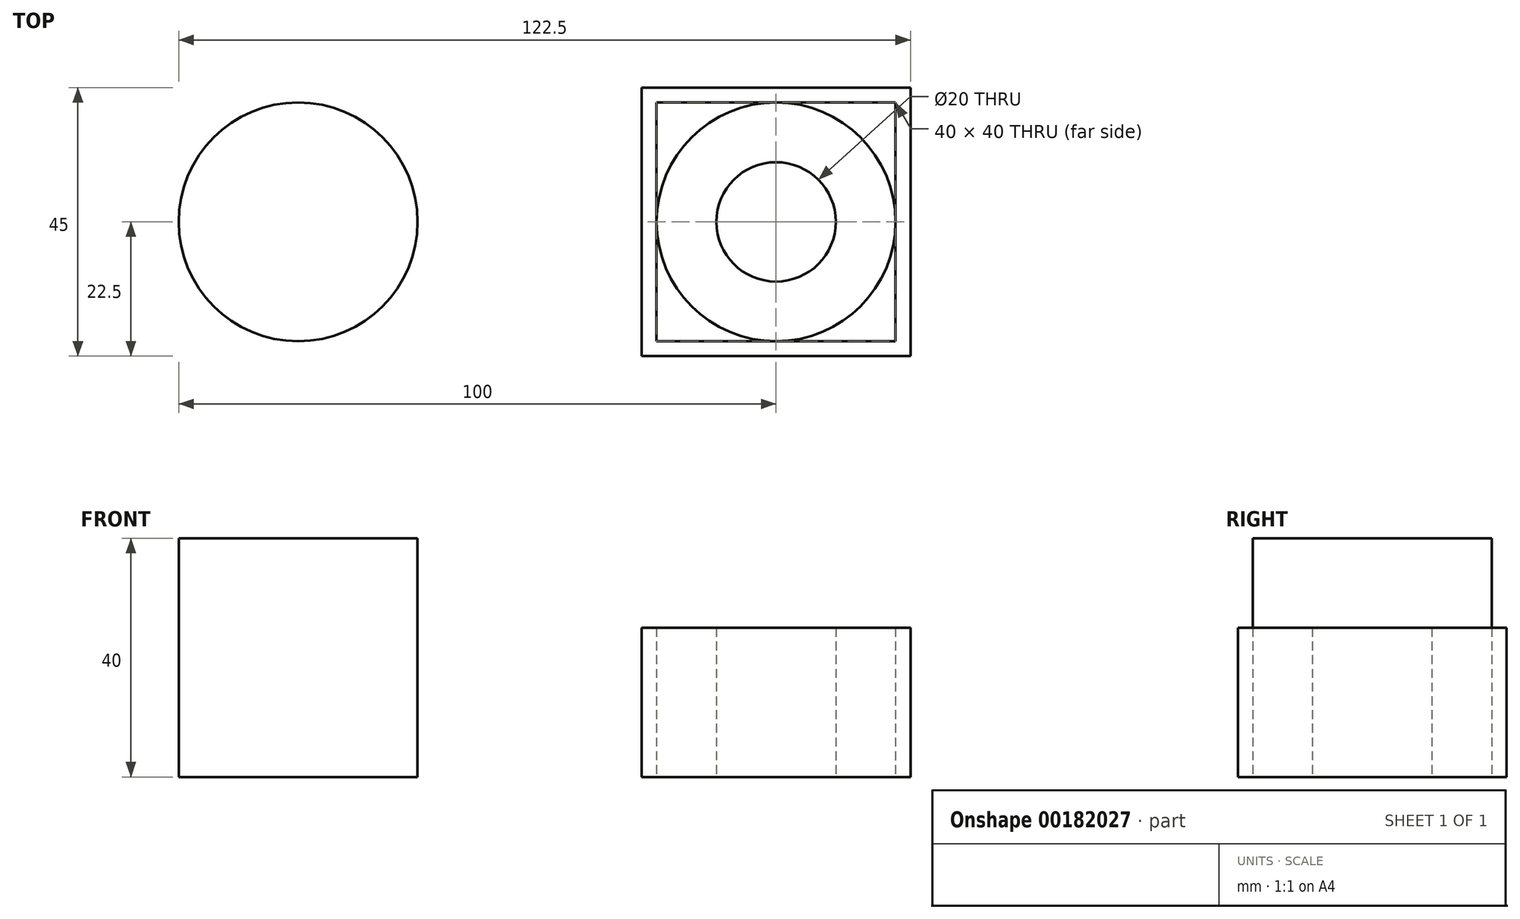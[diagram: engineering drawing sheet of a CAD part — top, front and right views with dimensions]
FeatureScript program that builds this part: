
annotation { "Feature Type Name" : "Feature", "Feature Type Description" : "" }
export const myFeature = defineFeature(function(context is Context, id is Id, definition is map)
    precondition{}
    {
        {
            var Q0;
            Q0=qCreatedBy(makeId("Top.planeOp"),FACE);
            var sketch = newSketch(context, id + "F0", { "sketchPlane" : qUnion([Q0])});
            skCircle(sketch, "E0", {"center": v(0, 0) * mm, "radius": 20 * mm});
            skCircle(sketch, "E1", {"center": v(80, 0) * mm, "radius": 20 * mm});
            skLineSegment(sketch, "E2.bottom", {"start": v(57.5, 22.5) * mm, "end": v(102.5, 22.5) * mm});
            skLineSegment(sketch, "E2.top", {"start": v(57.5, -22.5) * mm, "end": v(102.5, -22.5) * mm});
            skLineSegment(sketch, "E2.left", {"start": v(57.5, 22.5) * mm, "end": v(57.5, -22.5) * mm});
            skLineSegment(sketch, "E2.right", {"start": v(102.5, 22.5) * mm, "end": v(102.5, -22.5) * mm});
            skCircle(sketch, "E3", {"center": v(80, 0) * mm, "radius": 10 * mm});
            skLineSegment(sketch, "E4.bottom", {"start": v(60, 20) * mm, "end": v(100, 20) * mm});
            skLineSegment(sketch, "E4.top", {"start": v(60, -20) * mm, "end": v(100, -20) * mm});
            skLineSegment(sketch, "E4.left", {"start": v(60, 20) * mm, "end": v(60, -20) * mm});
            skLineSegment(sketch, "E4.right", {"start": v(100, 20) * mm, "end": v(100, -20) * mm});
            skSolve(sketch);
        }
        {
            var Q0;
            Q0=makeQuery(id+"F0.imprint","IMPRINT",FACE,{"disambiguationData":[TD([[makeQuery(id+"F0.imprint","IMPRINT",EDGE,{"derivedFrom":sQuery(id+"F0.wireOp",EDGE,"E0")}),1.0]])]});
            extrude(context, id + "F1", {"entities" : qUnion([Q0]), "depth" : 40 * mm});
        }
        {
            var Q0;
            Q0=makeQuery(id+"F0.imprint","IMPRINT",FACE,{"disambiguationData":[TD([[makeQuery(id+"F0.imprint","IMPRINT",EDGE,{"derivedFrom":sQuery(id+"F0.wireOp",EDGE,"E2.bottom")}),-1.0]])]});
            var Q1;
            Q1=makeQuery(id+"F0.imprint","IMPRINT",FACE,{"disambiguationData":[TD([[makeQuery(id+"F0.imprint","IMPRINT",EDGE,{"derivedFrom":sQuery(id+"F0.wireOp",EDGE,"E3")}),-1.0]])]});
            extrude(context, id + "F2", {"entities" : qUnion([Q0, Q1]), "depth" : 25 * mm});
        }
    });
